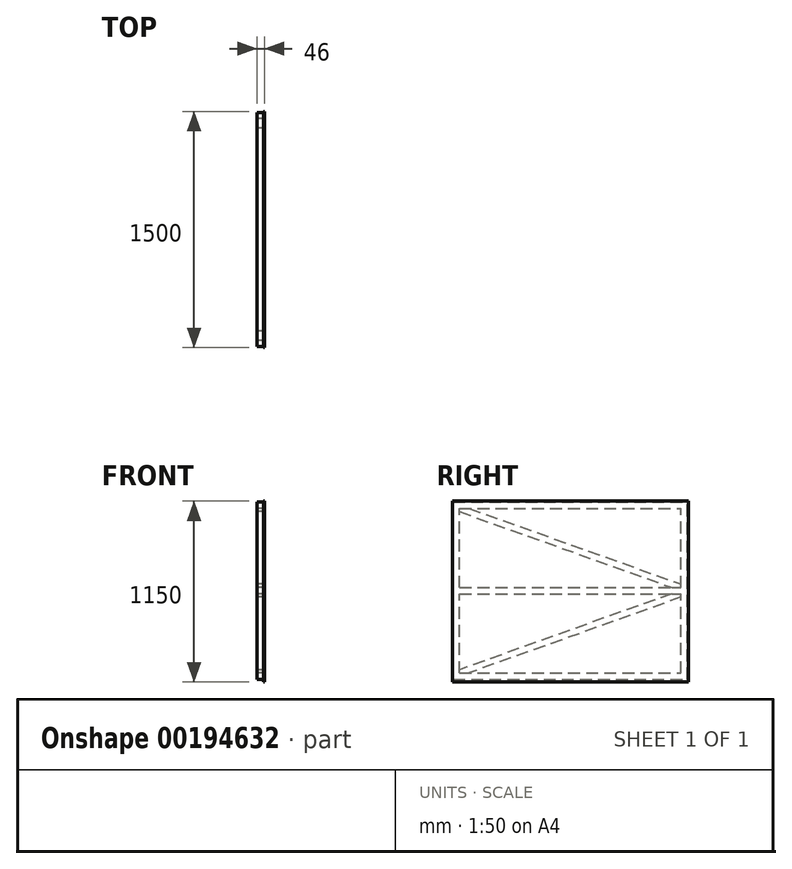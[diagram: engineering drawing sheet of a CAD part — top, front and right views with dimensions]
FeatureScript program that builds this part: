
annotation { "Feature Type Name" : "Feature", "Feature Type Description" : "" }
export const myFeature = defineFeature(function(context is Context, id is Id, definition is map)
    precondition{}
    {
        {
            var Q0;
            Q0=qCreatedBy(makeId("Right.planeOp"),FACE);
            var sketch = newSketch(context, id + "F0", { "sketchPlane" : qUnion([Q0])});
            skLineSegment(sketch, "E0.bottom", {"start": v(750, 575) * mm, "end": v(-750, 575) * mm});
            skLineSegment(sketch, "E0.top", {"start": v(750, -575) * mm, "end": v(-750, -575) * mm});
            skLineSegment(sketch, "E0.left", {"start": v(750, 575) * mm, "end": v(750, -575) * mm});
            skLineSegment(sketch, "E0.right", {"start": v(-750, 575) * mm, "end": v(-750, -575) * mm});
            skPoint(sketch, "E0.middle", {"position": v(0, 0) * mm});
            skSolve(sketch);
        }
        {
            var Q0;
            Q0 = qSketchRegion(id + "F0", true);
            extrude(context, id + "F1", {"entities" : qUnion([Q0]), "depth" : 6 * mm});
        }
        {
            var Q0;
            Q0=qCreatedBy(makeId("Front.planeOp"),FACE);
            var sketch = newSketch(context, id + "F2", { "sketchPlane" : qUnion([Q0])});
            skLineSegment(sketch, "E1.bottom", {"start": v(0, 569) * mm, "end": v(-40, 569) * mm});
            skLineSegment(sketch, "E1.top", {"start": v(0, 529) * mm, "end": v(-40, 529) * mm});
            skLineSegment(sketch, "E1.left", {"start": v(0, 569) * mm, "end": v(0, 529) * mm});
            skLineSegment(sketch, "E1.right", {"start": v(-40, 569) * mm, "end": v(-40, 529) * mm});
            skLineSegment(sketch, "E2.0.1.0", {"start": v(0, 26) * mm, "end": v(-40, 26) * mm});
            skLineSegment(sketch, "E2.0.1.1", {"start": v(-40, 26) * mm, "end": v(-40, -14) * mm});
            skLineSegment(sketch, "E2.0.1.2", {"start": v(0, 26) * mm, "end": v(0, -14) * mm});
            skLineSegment(sketch, "E2.0.1.3", {"start": v(0, -14) * mm, "end": v(-40, -14) * mm});
            skLineSegment(sketch, "E2.direction1", {"start": v(-40, 569) * mm, "end": v(-15, 569) * mm, "construction": true});
            skLineSegment(sketch, "E2.direction2", {"start": v(-40, 569) * mm, "end": v(-40, 26) * mm, "construction": true});
            skLineSegment(sketch, "E3.0.0.2", {"start": v(0, -517) * mm, "end": v(-40, -517) * mm});
            skLineSegment(sketch, "E3.3.0.2", {"start": v(-40, -517) * mm, "end": v(-40, -557) * mm});
            skLineSegment(sketch, "E3.6.0.2", {"start": v(0, -517) * mm, "end": v(0, -557) * mm});
            skLineSegment(sketch, "E3.9.0.2", {"start": v(0, -557) * mm, "end": v(-40, -557) * mm});
            skSolve(sketch);
        }
        {
            var Q0;
            Q0 = qSketchRegion(id + "F2", true);
            extrude(context, id + "F3", {"entities" : qUnion([Q0]), "operationType" : NewBodyOperationType.ADD, "endBound" : BoundingType.SYMMETRIC, "depth" : 1408 * mm});
        }
        {
            var Q0;
            Q0=makeQuery(id+"F3.opExtrude","SWEPT_FACE",FACE,{"disambiguationData":[OSD([sQuery(id+"F2.wireOp",EDGE,"E1.bottom")])]});
            var sketch = newSketch(context, id + "F4", { "sketchPlane" : qUnion([Q0])});
            skLineSegment(sketch, "E4.bottom", {"start": v(0, -704) * mm, "end": v(-40, -704) * mm});
            skLineSegment(sketch, "E4.top", {"start": v(0, -744) * mm, "end": v(-40, -744) * mm});
            skLineSegment(sketch, "E4.left", {"start": v(0, -704) * mm, "end": v(0, -744) * mm});
            skLineSegment(sketch, "E4.right", {"start": v(-40, -704) * mm, "end": v(-40, -744) * mm});
            skLineSegment(sketch, "E5.bottom", {"start": v(0, 704) * mm, "end": v(-40, 704) * mm});
            skLineSegment(sketch, "E5.top", {"start": v(0, 744) * mm, "end": v(-40, 744) * mm});
            skLineSegment(sketch, "E5.left", {"start": v(0, 704) * mm, "end": v(0, 744) * mm});
            skLineSegment(sketch, "E5.right", {"start": v(-40, 704) * mm, "end": v(-40, 744) * mm});
            skSolve(sketch);
        }
        {
            var Q0;
            Q0 = qSketchRegion(id + "F4", true);
            extrude(context, id + "F5", {"entities" : qUnion([Q0]), "operationType" : NewBodyOperationType.ADD, "oppositeDirection" : true, "depth" : 1126 * mm});
        }
        {
            var Q0;
            Q0=makeQuery(id+"F5.boolean.opBoolean","MERGE",FACE,{"derivedFrom":[makeQuery(id+"F3.opExtrude","SWEPT_FACE",FACE,{"disambiguationData":[OSD([sQuery(id+"F2.wireOp",EDGE,"E1.right")])]}),makeQuery(id+"F3.opExtrude","SWEPT_FACE",FACE,{"disambiguationData":[OSD([sQuery(id+"F2.wireOp",EDGE,"E2.0.1.1")])]}),makeQuery(id+"F3.opExtrude","SWEPT_FACE",FACE,{"disambiguationData":[OSD([sQuery(id+"F2.wireOp",EDGE,"E3.3.0.2")])]}),makeQuery(id+"F5.opExtrude","SWEPT_FACE",FACE,{"disambiguationData":[OSD([sQuery(id+"F4.wireOp",EDGE,"E4.right")])]}),makeQuery(id+"F5.opExtrude","SWEPT_FACE",FACE,{"disambiguationData":[OSD([sQuery(id+"F4.wireOp",EDGE,"E5.right")])]})]});
            var sketch = newSketch(context, id + "F6", { "sketchPlane" : qUnion([Q0])});
            skLineSegment(sketch, "E6.0", {"start": v(644.55, 529) * mm, "end": v(-704, 47.24) * mm});
            skLineSegment(sketch, "E7.0", {"start": v(704, 507.76) * mm, "end": v(-644.55, 26) * mm});
            skLineSegment(sketch, "E8.0", {"start": v(-704, -35.24) * mm, "end": v(644.55, -517) * mm});
            skLineSegment(sketch, "E9.0", {"start": v(-644.55, -14) * mm, "end": v(704, -495.76) * mm});
            skLineSegment(sketch, "E10", {"start": v(-704, 47.24) * mm, "end": v(-704, 26) * mm});
            skLineSegment(sketch, "E11", {"start": v(644.55, 529) * mm, "end": v(704, 529) * mm});
            skLineSegment(sketch, "E12", {"start": v(704, -495.76) * mm, "end": v(704, -517) * mm});
            skLineSegment(sketch, "E13", {"start": v(-704, -35.24) * mm, "end": v(-704, -14) * mm});
            skLineSegment(sketch, "E14", {"start": v(-704, 26) * mm, "end": v(-644.55, 26) * mm});
            skLineSegment(sketch, "E15", {"start": v(-704, -14) * mm, "end": v(-644.55, -14) * mm});
            skLineSegment(sketch, "E16", {"start": v(704, -517) * mm, "end": v(644.55, -517) * mm});
            skLineSegment(sketch, "E17", {"start": v(704, 507.76) * mm, "end": v(704, 529) * mm});
            skSolve(sketch);
        }
        {
            var Q0;
            Q0 = qSketchRegion(id + "F6", true);
            extrude(context, id + "F7", {"entities" : qUnion([Q0]), "oppositeDirection" : true, "depth" : 40 * mm});
        }
    });
